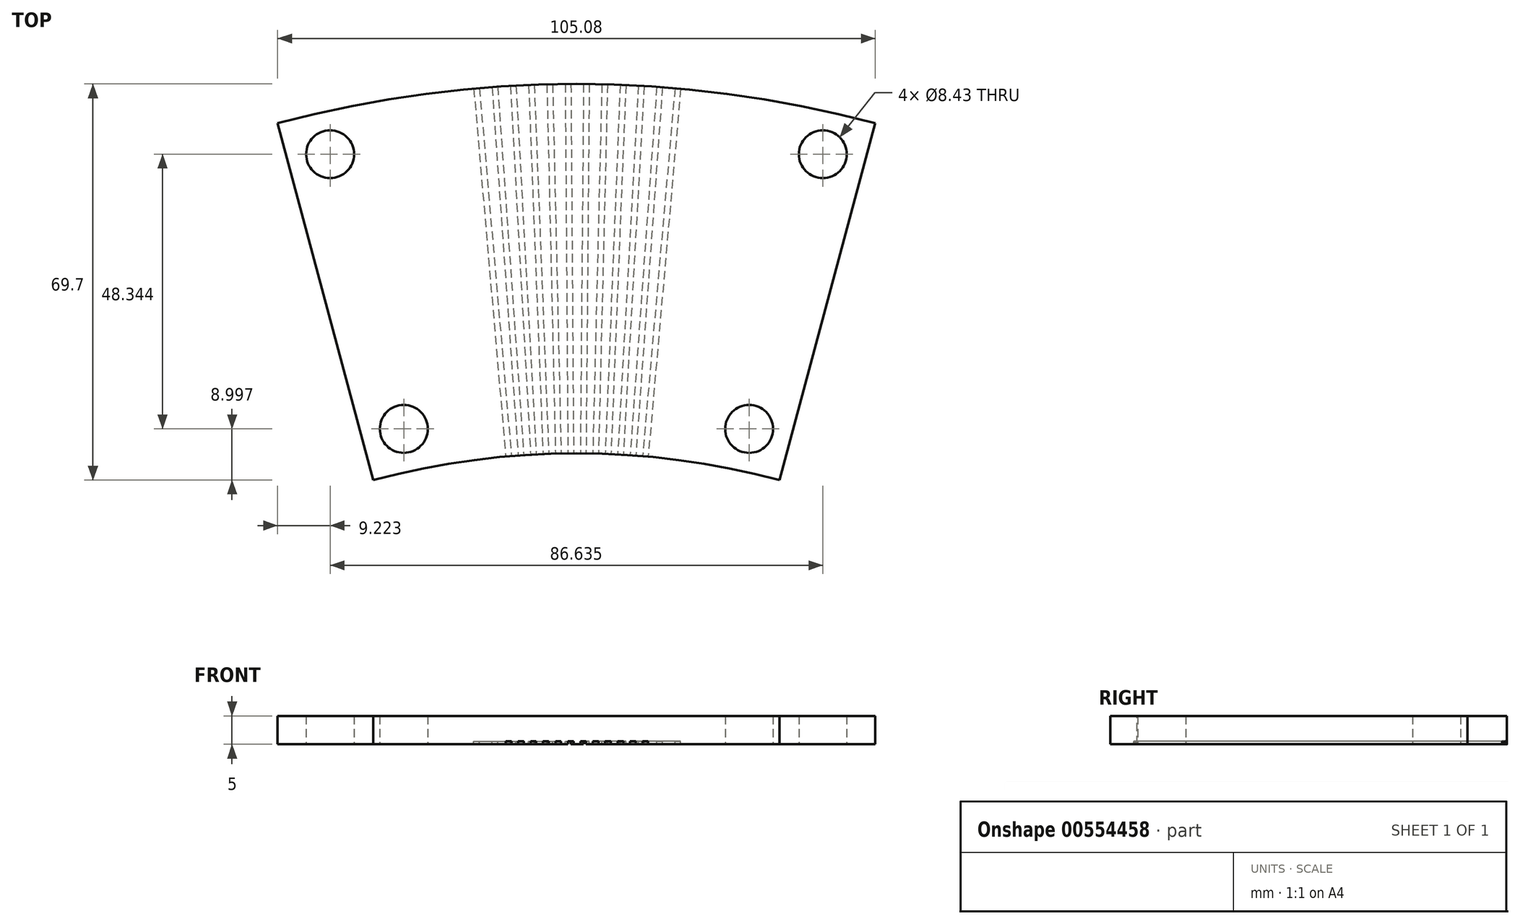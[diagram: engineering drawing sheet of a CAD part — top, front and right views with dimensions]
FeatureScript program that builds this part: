
annotation { "Feature Type Name" : "Feature", "Feature Type Description" : "" }
export const myFeature = defineFeature(function(context is Context, id is Id, definition is map)
    precondition{}
    {
        {
            var Q0;
            Q0=qCreatedBy(makeId("Right.planeOp"),FACE);
            var sketch = newSketch(context, id + "F0", { "sketchPlane" : qUnion([Q0])});
            skLineSegment(sketch, "E0", {"start": v(0, 0) * mm, "end": v(0, 5) * mm});
            skLineSegment(sketch, "E1", {"start": v(0, 5) * mm, "end": v(65, 5) * mm});
            skLineSegment(sketch, "E2", {"start": v(65, 5) * mm, "end": v(65, 0) * mm});
            skLineSegment(sketch, "E3", {"start": v(65, 0) * mm, "end": v(0, 0) * mm});
            skLineSegment(sketch, "E4", {"start": v(-138, 36.2) * mm, "end": v(-138, 0) * mm});
            skSolve(sketch);
        }
        {
            var Q0;
            Q0=makeQuery(id+"F0.imprint","IMPRINT",FACE,{"disambiguationData":[TD([[makeQuery(id+"F0.imprint","IMPRINT",EDGE,{"derivedFrom":sQuery(id+"F0.wireOp",EDGE,"E0")}),-1.0]])]});
            var Q1;
            Q1=sQuery(id+"F0.wireOp",EDGE,"E4");
            revolve(context, id + "F1", {"entities" : qUnion([Q0]), "axis" : qUnion([Q1]), "revolveType" : RevolveType.SYMMETRIC, "angle" : 30 * degree});
        }
        {
            var Q0;
            Q0=makeQuery(id+"F1.opRevolve","SWEPT_FACE",FACE,{"disambiguationData":[OSD([sQuery(id+"F0.wireOp",EDGE,"E3")])]});
            var sketch = newSketch(context, id + "F2", { "sketchPlane" : qUnion([Q0])});
            skPoint(sketch, "E5.middle", {"position": v(0, 0) * mm});
            skLineSegment(sketch, "E6", {"start": v(0, 0) * mm, "end": v(-11.98, 0) * mm});
            skLineSegment(sketch, "E7", {"start": v(-11.98, 0) * mm, "end": v(11.98, 0) * mm});
            skLineSegment(sketch, "E8.bottom", {"start": v(-22.84, -303.92) * mm, "end": v(-21.84, -303.92) * mm});
            skPoint(sketch, "E8.middle", {"position": v(-11.98, 0) * mm});
            skLineSegment(sketch, "E9.bottom", {"start": v(-18.72, -71.9) * mm, "end": v(-17.72, -71.98) * mm});
            skLineSegment(sketch, "E9.top", {"start": v(-6.23, 71.98) * mm, "end": v(-5.24, 71.9) * mm});
            skLineSegment(sketch, "E9.left", {"start": v(-18.72, -71.9) * mm, "end": v(-6.23, 71.98) * mm});
            skLineSegment(sketch, "E9.right", {"start": v(-17.72, -71.98) * mm, "end": v(-5.24, 71.9) * mm});
            skLineSegment(sketch, "E10", {"start": v(-11.98, 0) * mm, "end": v(0, 138) * mm});
            skLineSegment(sketch, "E11.1.0", {"start": v(-15.39, -72.16) * mm, "end": v(-14.4, -72.23) * mm});
            skLineSegment(sketch, "E11.1.1", {"start": v(-15.39, -72.16) * mm, "end": v(-5.18, 71.89) * mm});
            skLineSegment(sketch, "E11.1.2", {"start": v(-14.4, -72.23) * mm, "end": v(-4.19, 71.82) * mm});
            skLineSegment(sketch, "E11.1.3", {"start": v(-5.18, 71.89) * mm, "end": v(-4.19, 71.82) * mm});
            skLineSegment(sketch, "E11.2.0", {"start": v(-12.05, -72.38) * mm, "end": v(-11.05, -72.43) * mm});
            skLineSegment(sketch, "E11.2.1", {"start": v(-12.05, -72.38) * mm, "end": v(-4.13, 71.81) * mm});
            skLineSegment(sketch, "E11.2.2", {"start": v(-11.05, -72.43) * mm, "end": v(-3.14, 71.76) * mm});
            skLineSegment(sketch, "E11.2.3", {"start": v(-4.13, 71.81) * mm, "end": v(-3.14, 71.76) * mm});
            skLineSegment(sketch, "E11.3.0", {"start": v(-8.71, -72.54) * mm, "end": v(-7.71, -72.58) * mm});
            skLineSegment(sketch, "E11.3.1", {"start": v(-8.71, -72.54) * mm, "end": v(-3.08, 71.76) * mm});
            skLineSegment(sketch, "E11.3.2", {"start": v(-7.71, -72.58) * mm, "end": v(-2.08, 71.72) * mm});
            skLineSegment(sketch, "E11.3.3", {"start": v(-3.08, 71.76) * mm, "end": v(-2.08, 71.72) * mm});
            skLineSegment(sketch, "E11.4.0", {"start": v(-5.37, -72.66) * mm, "end": v(-4.37, -72.68) * mm});
            skLineSegment(sketch, "E11.4.1", {"start": v(-5.37, -72.66) * mm, "end": v(-2.03, 71.71) * mm});
            skLineSegment(sketch, "E11.4.2", {"start": v(-4.37, -72.68) * mm, "end": v(-1.03, 71.7) * mm});
            skLineSegment(sketch, "E11.4.3", {"start": v(-2.03, 71.71) * mm, "end": v(-1.03, 71.7) * mm});
            skLineSegment(sketch, "E11.5.0", {"start": v(-2.03, -72.71) * mm, "end": v(-1.03, -72.72) * mm});
            skLineSegment(sketch, "E11.5.1", {"start": v(-2.03, -72.71) * mm, "end": v(-0.98, 71.7) * mm});
            skLineSegment(sketch, "E11.5.2", {"start": v(-1.03, -72.72) * mm, "end": v(0.02, 71.68) * mm});
            skLineSegment(sketch, "E11.5.3", {"start": v(-0.98, 71.7) * mm, "end": v(0.02, 71.68) * mm});
            skLineSegment(sketch, "E11.6.0", {"start": v(1.32, -72.72) * mm, "end": v(2.32, -72.71) * mm});
            skLineSegment(sketch, "E11.6.1", {"start": v(1.32, -72.72) * mm, "end": v(0.07, 71.68) * mm});
            skLineSegment(sketch, "E11.6.2", {"start": v(2.32, -72.71) * mm, "end": v(1.07, 71.7) * mm});
            skLineSegment(sketch, "E11.6.3", {"start": v(0.07, 71.68) * mm, "end": v(1.07, 71.7) * mm});
            skLineSegment(sketch, "E11.7.0", {"start": v(4.66, -72.67) * mm, "end": v(5.66, -72.65) * mm});
            skLineSegment(sketch, "E11.7.1", {"start": v(4.66, -72.67) * mm, "end": v(1.12, 71.7) * mm});
            skLineSegment(sketch, "E11.7.2", {"start": v(5.66, -72.65) * mm, "end": v(2.12, 71.72) * mm});
            skLineSegment(sketch, "E11.7.3", {"start": v(1.12, 71.7) * mm, "end": v(2.12, 71.72) * mm});
            skLineSegment(sketch, "E11.8.0", {"start": v(8, -72.57) * mm, "end": v(9, -72.53) * mm});
            skLineSegment(sketch, "E11.8.1", {"start": v(8, -72.57) * mm, "end": v(2.18, 71.72) * mm});
            skLineSegment(sketch, "E11.8.2", {"start": v(9, -72.53) * mm, "end": v(3.17, 71.76) * mm});
            skLineSegment(sketch, "E11.8.3", {"start": v(2.18, 71.72) * mm, "end": v(3.17, 71.76) * mm});
            skLineSegment(sketch, "E11.9.0", {"start": v(11.34, -72.42) * mm, "end": v(12.34, -72.36) * mm});
            skLineSegment(sketch, "E11.9.1", {"start": v(11.34, -72.42) * mm, "end": v(3.23, 71.76) * mm});
            skLineSegment(sketch, "E11.9.2", {"start": v(12.34, -72.36) * mm, "end": v(4.23, 71.82) * mm});
            skLineSegment(sketch, "E11.9.3", {"start": v(3.23, 71.76) * mm, "end": v(4.23, 71.82) * mm});
            skLineSegment(sketch, "E11.10.0", {"start": v(14.68, -72.21) * mm, "end": v(15.68, -72.14) * mm});
            skLineSegment(sketch, "E11.10.1", {"start": v(14.68, -72.21) * mm, "end": v(4.28, 71.82) * mm});
            skLineSegment(sketch, "E11.10.2", {"start": v(15.68, -72.14) * mm, "end": v(5.27, 71.9) * mm});
            skLineSegment(sketch, "E11.10.3", {"start": v(4.28, 71.82) * mm, "end": v(5.27, 71.9) * mm});
            skLineSegment(sketch, "E11.11.0", {"start": v(18.01, -71.95) * mm, "end": v(19, -71.86) * mm});
            skLineSegment(sketch, "E11.11.1", {"start": v(18.01, -71.95) * mm, "end": v(5.33, 71.9) * mm});
            skLineSegment(sketch, "E11.11.2", {"start": v(19, -71.86) * mm, "end": v(6.32, 71.99) * mm});
            skLineSegment(sketch, "E11.11.3", {"start": v(5.33, 71.9) * mm, "end": v(6.32, 71.99) * mm});
            skPoint(sketch, "E11.center", {"position": v(0, 138) * mm});
            skLineSegment(sketch, "E11.anchor1", {"start": v(0, 138) * mm, "end": v(-5.24, 71.9) * mm, "construction": true});
            skLineSegment(sketch, "E11.anchor2", {"start": v(0, 138) * mm, "end": v(6.32, 71.99) * mm, "construction": true});
            skSolve(sketch);
        }
        {
            var Q0;
            Q0 = qSketchRegion(id + "F2", true);
            extrude(context, id + "F3", {"entities" : qUnion([Q0]), "operationType" : NewBodyOperationType.REMOVE, "oppositeDirection" : true, "depth" : .5 * mm, "offsetDistance" : 25 * mm});
        }
        {
            var Q0;
            {var subQ1=sQuery(id+"F0.wireOp",EDGE,"E3");Q0=makeQuery(id+"F3.boolean.opBoolean","SPLIT",FACE,{"disambiguationData":[TD([makeQuery(id+"F3.opExtrude","SWEPT_FACE",FACE,{"disambiguationData":[OSD([sQuery(id+"F2.wireOp",EDGE,"E11.11.2")])]})])],"derivedFrom":makeQuery(id+"F1.opRevolve","SWEPT_FACE",FACE,{"disambiguationData":[OSD([subQ1])]})});}
            var sketch = newSketch(context, id + "F4", { "sketchPlane" : qUnion([Q0])});
            skCircle(sketch, "E12", {"center": v(30.36, -4.3) * mm, "radius": 7.5 * mm});
            skCircle(sketch, "E13", {"center": v(-30.36, -4.3) * mm, "radius": 7.5 * mm});
            skCircle(sketch, "E14", {"center": v(-43.32, -52.64) * mm, "radius": 7.5 * mm});
            skCircle(sketch, "E15", {"center": v(43.32, -52.64) * mm, "radius": 7.5 * mm});
            skSolve(sketch);
        }
        {
            var Q0;
            Q0=sQuery(id+"F4.wireOp",VERTEX,"E13.center");
            var Q1;
            Q1=sQuery(id+"F4.wireOp",VERTEX,"E12.center");
            var Q2;
            Q2=sQuery(id+"F4.wireOp",VERTEX,"E15.center");
            var Q3;
            Q3=sQuery(id+"F4.wireOp",VERTEX,"E14.center");
            var Q4;
            Q4=makeQuery(id+"F1.opRevolve","SWEPT_BODY",BODY,{"disambiguationData":[OSD([sQuery(id+"F0.wireOp",EDGE,"E0"),sQuery(id+"F0.wireOp",EDGE,"E1"),sQuery(id+"F0.wireOp",EDGE,"E2"),sQuery(id+"F0.wireOp",EDGE,"E3")])]});
            hole(context, id + "F5", {"style" : HoleStyle.SIMPLE, "endStyle" : HoleEndStyle.THROUGH, "standardTappedOrClearance" : lookupTablePath({ "standard" : "ANSI", "fit" : "Normal (ASME)", "size" : "5/16", "type" : "Clearance" }), "standardBlindInLast" : lookupTablePath({ "fit" : "Free", "standard" : "ANSI", "size" : "5/16", "type" : "Clearance" }), "holeDiameter" : 8.43 * mm, "isTappedThrough" : true, "tappedDepth" : 12 * mm, "tapClearance" : 3, "locations" : qUnion([Q0, Q1, Q2, Q3]), "scope" : qUnion([Q4])});
        }
    });
